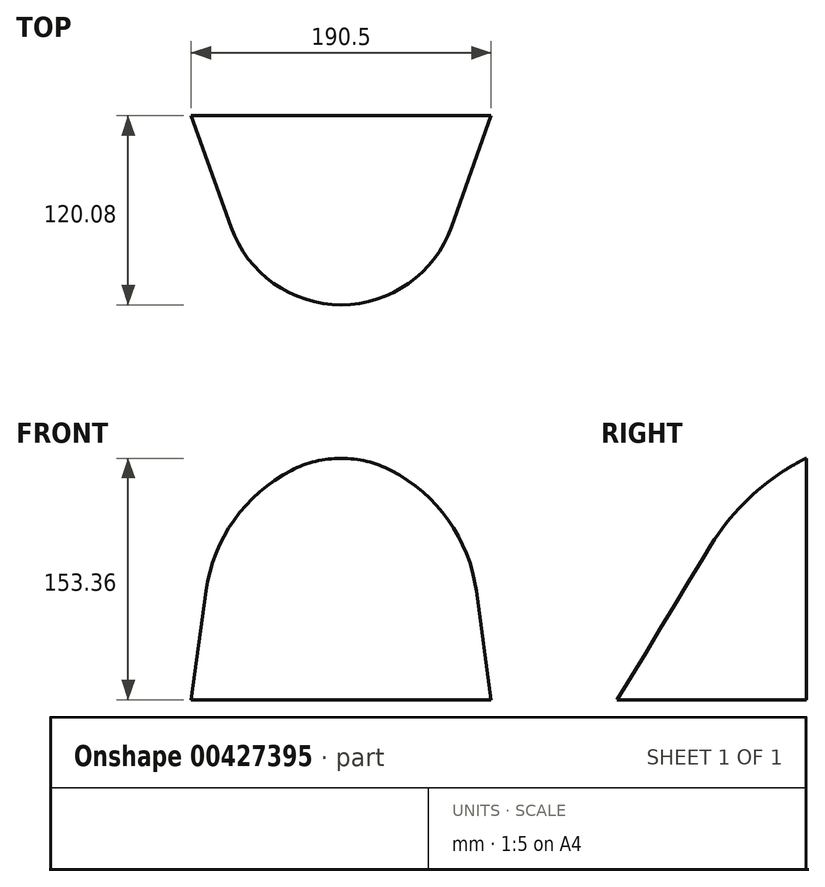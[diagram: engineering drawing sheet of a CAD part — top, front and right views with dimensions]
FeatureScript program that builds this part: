
annotation { "Feature Type Name" : "Feature", "Feature Type Description" : "" }
export const myFeature = defineFeature(function(context is Context, id is Id, definition is map)
    precondition{}
    {
        {
            var Q0;
            Q0=qCreatedBy(makeId("Front.planeOp"),FACE);
            var sketch = newSketch(context, id + "F0", { "sketchPlane" : qUnion([Q0])});
            skLineSegment(sketch, "E0", {"start": v(0, 153.36) * mm, "end": v(0, 0) * mm, "construction": true});
            skLineSegment(sketch, "E1", {"start": v(0, 0) * mm, "end": v(95.25, 0) * mm});
            skLineSegment(sketch, "E2", {"start": v(95.25, 0) * mm, "end": v(85.8, 69.13) * mm});
            skArc(sketch, "E3", {"start": v(85.8, 69.13) * mm, "mid": v(68.09, 114.03) * mm, "end": v(31.65, 145.7) * mm});
            skArc(sketch, "E4", {"start": v(31.65, 145.7) * mm, "mid": v(16.28, 151.41) * mm, "end": v(0, 153.36) * mm});
            skArc(sketch, "E5.MirrorCS", {"start": v(-85.8, 69.13) * mm, "mid": v(-68.09, 114.03) * mm, "end": v(-31.65, 145.7) * mm});
            skLineSegment(sketch, "E6.MirrorCS", {"start": v(-95.25, 0) * mm, "end": v(-85.8, 69.13) * mm});
            skLineSegment(sketch, "E7.MirrorCS", {"start": v(0, 0) * mm, "end": v(-95.25, 0) * mm});
            skArc(sketch, "E8", {"start": v(0, 153.36) * mm, "mid": v(-16.28, 151.41) * mm, "end": v(-31.65, 145.7) * mm});
            skSolve(sketch);
        }
        {
            var Q0;
            Q0=qCreatedBy(makeId("Top.planeOp"),FACE);
            var sketch = newSketch(context, id + "F1", { "sketchPlane" : qUnion([Q0])});
            skLineSegment(sketch, "E9", {"start": v(-95.25, 0) * mm, "end": v(-70.05, -70.7) * mm});
            skArc(sketch, "E10", {"start": v(-70.05, -70.7) * mm, "mid": v(0, -120.08) * mm, "end": v(70.05, -70.7) * mm});
            skLineSegment(sketch, "E11", {"start": v(0, -4.05) * mm, "end": v(0, -115.34) * mm, "construction": true});
            skLineSegment(sketch, "E12", {"start": v(-95.25, 0) * mm, "end": v(95.25, 0) * mm});
            skLineSegment(sketch, "E13.MirrorCS", {"start": v(95.25, 0) * mm, "end": v(70.05, -70.7) * mm});
            skSolve(sketch);
        }
        {
            var Q0;
            Q0=qCreatedBy(makeId("Right.planeOp"),FACE);
            var sketch = newSketch(context, id + "F2", { "sketchPlane" : qUnion([Q0])});
            skArc(sketch, "E14", {"start": v(0, 153.36) * mm, "mid": v(-34.3, 129.9) * mm, "end": v(-60.67, 97.8) * mm});
            skLineSegment(sketch, "E15", {"start": v(-60.67, 97.8) * mm, "end": v(-120.08, 0) * mm});
            skSolve(sketch);
        }
        {
            var Q0;
            Q0=qCreatedBy(makeId("Front.planeOp"),FACE);
            var sketch = newSketch(context, id + "F3", { "sketchPlane" : qUnion([Q0])});
            skLineSegment(sketch, "E16.0", {"start": v(-95.25, 0) * mm, "end": v(-85.8, 69.13) * mm});
            skArc(sketch, "E16.1", {"start": v(-85.8, 69.13) * mm, "mid": v(-68.09, 114.03) * mm, "end": v(-31.65, 145.7) * mm});
            skArc(sketch, "E16.2", {"start": v(0, 153.36) * mm, "mid": v(-16.28, 151.41) * mm, "end": v(-31.65, 145.7) * mm});
            skSolve(sketch);
        }
        {
            var Q0;
            Q0=qCreatedBy(makeId("Front.planeOp"),FACE);
            var sketch = newSketch(context, id + "F4", { "sketchPlane" : qUnion([Q0])});
            skLineSegment(sketch, "E17.0", {"start": v(95.25, 0) * mm, "end": v(85.8, 69.13) * mm});
            skArc(sketch, "E17.1", {"start": v(85.8, 69.13) * mm, "mid": v(68.09, 114.03) * mm, "end": v(31.65, 145.7) * mm});
            skArc(sketch, "E17.2", {"start": v(31.65, 145.7) * mm, "mid": v(16.28, 151.41) * mm, "end": v(0, 153.36) * mm});
            skSolve(sketch);
        }
        {
            var Q0;
            Q0=makeQuery(id+"F1.imprint","IMPRINT",FACE,{"disambiguationData":[TD([[makeQuery(id+"F1.imprint","IMPRINT",EDGE,{"derivedFrom":sQuery(id+"F1.wireOp",EDGE,"E9")}),1.0]])]});
            var Q1;
            Q1=sQuery(id+"F4.wireOp",VERTEX,"E17.2.end");
            var Q2;
            Q2 = qConstructionFilter(qBodyType(qCreatedBy(id + "F2" ,EDGE), BodyType.WIRE), ConstructionObject.NO);
            var Q3;
            Q3 = qConstructionFilter(qBodyType(qCreatedBy(id + "F3" ,EDGE), BodyType.WIRE), ConstructionObject.NO);
            var Q4;
            Q4 = qConstructionFilter(qBodyType(qCreatedBy(id + "F4" ,EDGE), BodyType.WIRE), ConstructionObject.NO);
            loft(context, id + "F5", {"addGuides" : true, "sheetProfilesArray" : [{ "sheetProfileEntities" : qUnion([Q0]) }, { "sheetProfileEntities" : qUnion([Q1]) }], "guidesArray" : [{ "guideEntities" : qUnion([Q2]), "guideDerivativeType" : LoftGuideDerivativeType.DEFAULT, "guideDerivativeMagnitude" : 1 }, { "guideEntities" : qUnion([Q3]), "guideDerivativeType" : LoftGuideDerivativeType.DEFAULT, "guideDerivativeMagnitude" : 1 }, { "guideEntities" : qUnion([Q4]), "guideDerivativeType" : LoftGuideDerivativeType.DEFAULT, "guideDerivativeMagnitude" : 1 }]});
        }
    });
